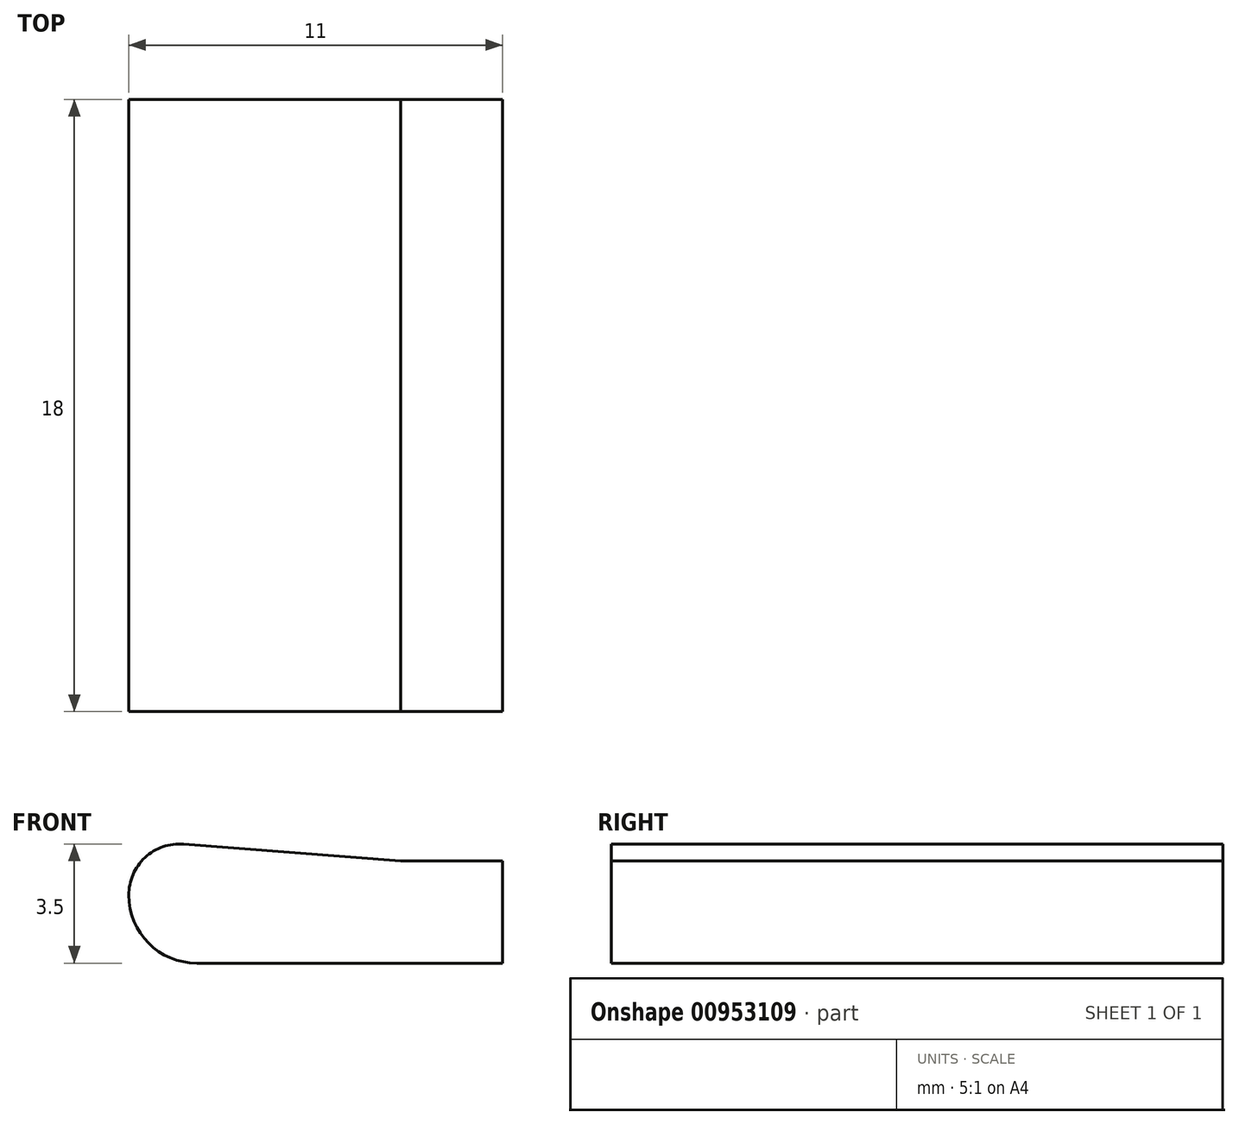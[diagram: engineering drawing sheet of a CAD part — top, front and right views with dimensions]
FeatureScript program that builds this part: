
annotation { "Feature Type Name" : "Feature", "Feature Type Description" : "" }
export const myFeature = defineFeature(function(context is Context, id is Id, definition is map)
    precondition{}
    {
        {
            var Q0;
            Q0=qCreatedBy(makeId("Front.planeOp"),FACE);
            var sketch = newSketch(context, id + "F0", { "sketchPlane" : qUnion([Q0])});
            skLineSegment(sketch, "E0", {"start": v(0, 0) * mm, "end": v(0, 3) * mm});
            skLineSegment(sketch, "E1", {"start": v(0, 0) * mm, "end": v(-6, 0) * mm});
            skLineSegment(sketch, "E2", {"start": v(0, 3) * mm, "end": v(-6.38, 3.5) * mm});
            skArc(sketch, "E3", {"start": v(-6.38, 3.5) * mm, "mid": v(-7.52, 3.1) * mm, "end": v(-8, 2) * mm});
            skArc(sketch, "E4", {"start": v(-8, 2) * mm, "mid": v(-7.41, 0.59) * mm, "end": v(-6, 0) * mm});
            skSolve(sketch);
        }
        {
            var Q0;
            Q0=makeQuery(id+"F0.imprint","IMPRINT",FACE,{"disambiguationData":[TD([[makeQuery(id+"F0.imprint","IMPRINT",EDGE,{"derivedFrom":sQuery(id+"F0.wireOp",EDGE,"E0")}),1.0]])]});
            extrude(context, id + "F1", {"entities" : qUnion([Q0]), "depth" : 60 * mm, "offsetDistance" : 25 * mm});
        }
        {
            var Q0;
            Q0=makeQuery(id+"F1.opExtrude","CAP_FACE",FACE,{"disambiguationData":[OSD([sQuery(id+"F0.wireOp",EDGE,"E0"),sQuery(id+"F0.wireOp",EDGE,"E1"),sQuery(id+"F0.wireOp",EDGE,"E2"),sQuery(id+"F0.wireOp",EDGE,"E3"),sQuery(id+"F0.wireOp",EDGE,"E4")])],"isStart":false});
            var sketch = newSketch(context, id + "F2", { "sketchPlane" : qUnion([Q0])});
            skLineSegment(sketch, "E5.bottom", {"start": v(0, 3) * mm, "end": v(3, 3) * mm});
            skLineSegment(sketch, "E5.top", {"start": v(0, 0) * mm, "end": v(3, 0) * mm});
            skLineSegment(sketch, "E5.left", {"start": v(0, 3) * mm, "end": v(0, 0) * mm});
            skLineSegment(sketch, "E5.right", {"start": v(3, 3) * mm, "end": v(3, 0) * mm});
            skSolve(sketch);
        }
        {
            var Q0;
            Q0 = qSketchRegion(id + "F2", true);
            extrude(context, id + "F3", {"entities" : qUnion([Q0]), "operationType" : NewBodyOperationType.ADD, "depth" : -60 * mm, "offsetDistance" : 25 * mm});
        }
        {
            var Q0;
            Q0=makeQuery(id+"F3.boolean.opBoolean","MERGE",FACE,{"derivedFrom":[makeQuery(id+"F1.opExtrude","CAP_FACE",FACE,{"disambiguationData":[OSD([sQuery(id+"F0.wireOp",EDGE,"E0"),sQuery(id+"F0.wireOp",EDGE,"E1"),sQuery(id+"F0.wireOp",EDGE,"E2"),sQuery(id+"F0.wireOp",EDGE,"E3"),sQuery(id+"F0.wireOp",EDGE,"E4")])],"isStart":false}),makeQuery(id+"F3.opExtrude","CAP_FACE",FACE,{"disambiguationData":[OSD([sQuery(id+"F2.wireOp",EDGE,"E5.bottom"),sQuery(id+"F2.wireOp",EDGE,"E5.top"),sQuery(id+"F2.wireOp",EDGE,"E5.left"),sQuery(id+"F2.wireOp",EDGE,"E5.right")])],"isStart":true})]});
            extrude(context, id + "F4", {"entities" : qUnion([Q0]), "operationType" : NewBodyOperationType.REMOVE, "oppositeDirection" : true, "depth" : 42 * mm, "offsetDistance" : 25 * mm});
        }
    });
